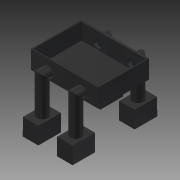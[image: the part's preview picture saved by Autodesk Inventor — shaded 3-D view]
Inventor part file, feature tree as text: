
AUTODESK INVENTOR PART (.ipt)
format: ipt  version: 2015 (Build 190159000, 159)  size: 910,848 bytes
history: native  units: in
note: dims shown in document units (in); Inventor stores cm internally (conversion verified against a paired STEP export)
features: sketch x8, extrude x7, plane x5, mirror x3, other x3, sweep x1, fillet x1, projected_geometry x1
ambient origin geometry x8: Origin, YZ Plane, XZ Plane, XY Plane, X Axis, Y Axis, Z Axis, Center Point
bodies: body (feature_tree), Solid6 (feature_tree), Solid7 (feature_tree), Solid8 (feature_tree)
feature tree (29):
  extrude  "Extrusion1"  Depth=36.0in
  extrude  "Extrusion2"  Depth=1.0in
  sketch  "Sketch3"  dims[d5=12.0in d6=0.0in d8=3.75in]
  extrude  "Extrusion4"  Depth=3.75in
  sweep  "Sweep1"
  plane  "Work Plane1"
  plane  "Work Plane2"
  plane  "Work Plane3"
  sketch  "Sketch5"  dims[d14=6.0in d15=41.3125in d16=0.0in]
  extrude  "Extrusion5"  Depth=41.3125in TaperAngle=0.0deg
  extrude  "Extrusion7"  Depth=24.0in
  extrude  "Extrusion8"  Depth=0.4in
  extrude  "Extrusion9"  Depth=0.4in
  mirror  "Mirror4"
  mirror  "Mirror5"
  mirror  "Mirror6"
  fillet  "Fillet6"  Radius=11.0in
  plane  "Work Plane5"
  sketch  "Sketch1"  dims[d0=48.0in d1=36.0in]
  sketch  "Sketch2"  dims[d2=1.0in d3=0.0in d4=1.0in]
  projected_geometry  "Projected Loop1"
  sketch  "Sketch4"  dims[d12=4.0in d13=6.0in]
  sketch  "3D Sketch1"
  sketch  "Sketch6"  dims[d17=0.0in d18=0.0in d19=-18.0in d20=24.0in]
  sketch  "Sketch7"  dims[d21=0.0in d22=11.0in d23=16.0in d24=11.0in d25=0.0in d28=1.0in d29=0.0in d30=1.0in d31=10.0in d32=0.0in d33=1.0in d34=0.0in d43=0.4in d44=-7.1875in]
  other  "Pattern of L4:4"
  other  "Pattern of Solid6:5"
  other  "Pattern of L4:6"
  plane  "Work Plane4"
